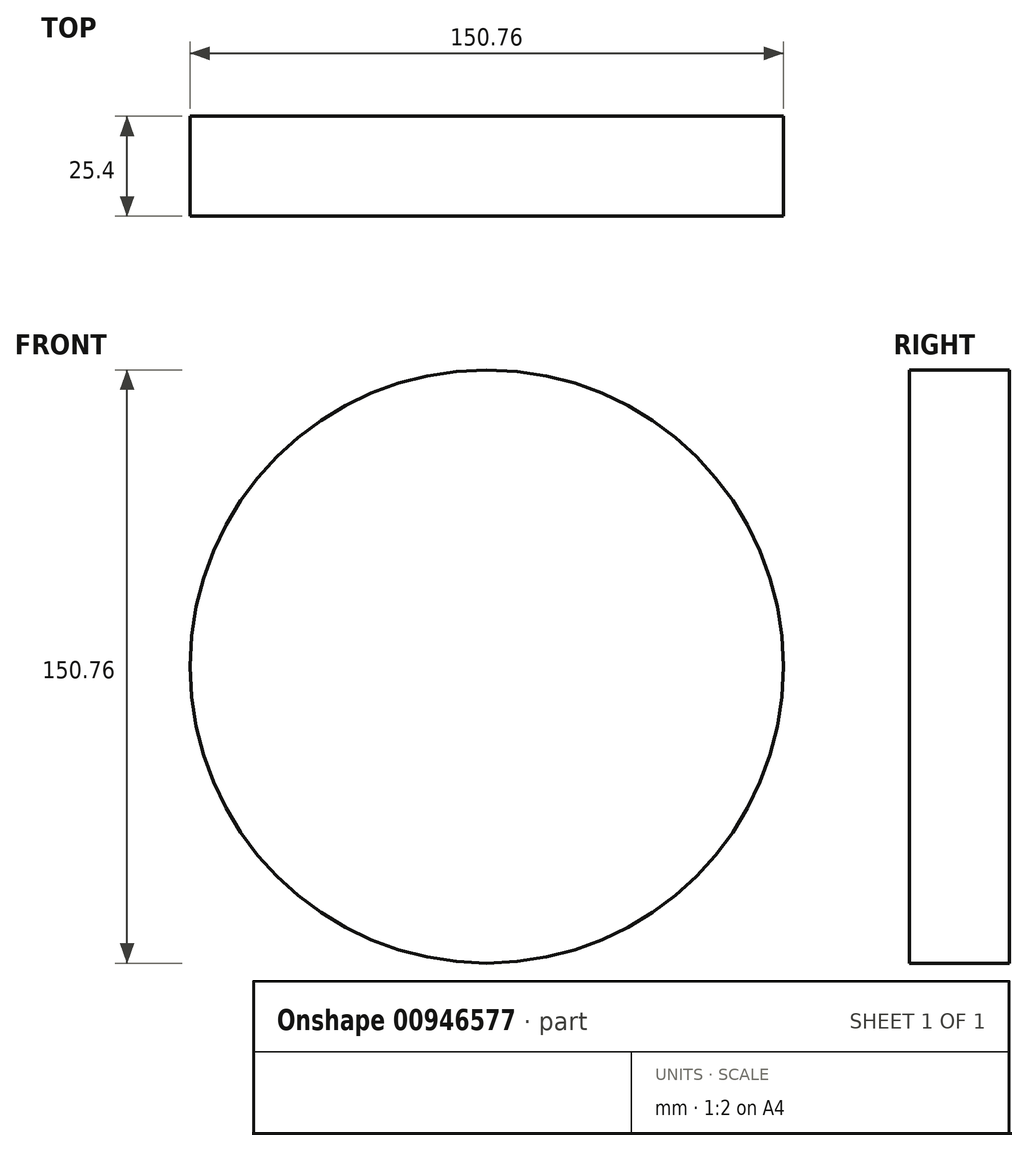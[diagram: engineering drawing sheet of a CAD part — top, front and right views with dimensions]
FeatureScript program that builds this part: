
annotation { "Feature Type Name" : "Feature", "Feature Type Description" : "" }
export const myFeature = defineFeature(function(context is Context, id is Id, definition is map)
    precondition{}
    {
        {
            var Q0;
            Q0=qCreatedBy(makeId("Front.planeOp"),FACE);
            var sketch = newSketch(context, id + "F0", { "sketchPlane" : qUnion([Q0])});
            skCircle(sketch, "E0", {"center": v(0, 0) * mm, "radius": 75.38 * mm});
            skSolve(sketch);
        }
        {
            var Q0;
            Q0=makeQuery(id+"F0.imprint","IMPRINT",FACE,{"disambiguationData":[TD([[makeQuery(id+"F0.imprint","IMPRINT",EDGE,{"derivedFrom":sQuery(id+"F0.wireOp",EDGE,"E0")}),1.0]])]});
            extrude(context, id + "F1", {"entities" : qUnion([Q0]), "depth" : 25.4 * mm, "offsetDistance" : 25.4 * mm});
        }
    });
